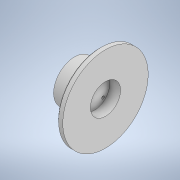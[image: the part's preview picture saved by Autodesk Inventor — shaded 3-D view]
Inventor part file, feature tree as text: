
AUTODESK INVENTOR PART (.ipt)
format: ipt  version: 2021 (Build 250183000, 183)  size: 325,120 bytes
history: native  units: mm
features: sketch x3, extrude x2, revolve x1, plane x1, pattern_circular x1
ambient origin geometry x8: Origin, YZ Plane, XZ Plane, XY Plane, X Axis, Y Axis, Z Axis, Center Point
bodies: Solid1 (feature_tree)
feature tree (8):
  revolve  "Revolution1"  [1 undecoded]
  plane  "Work Plane1"
  extrude  "Extrusion1"  Depth=2.0mm
  pattern_circular  "Circular Pattern1"  [2 undecoded]
  extrude  "Extrusion2"  Depth=10.0mm
  sketch  "Sketch1"  dims[d0=25.0mm d1=30.0mm]
  sketch  "Sketch2"  dims[d2=2.0mm d3=2.0mm]
  sketch  "Sketch3"  dims[d4=2.0mm d5=4.0mm d6=5.0mm d7=45.0mm d8=18.0mm d9=24.0mm d10=90.0deg d11=30.0mm d12=3.0mm d13=1.0mm d14=1.0mm d15=1.0mm d16=0.0mm d17=0.0mm d18=360.0mm d19=360.0deg d21=20.0mm d22=20.0mm d23=10.0mm d24=10.0mm d25=3.2mm d27=0.0mm d28=0.0mm]
note: 3 required parameter values undecoded (feature->parameter linkage not recoverable at this tier; creation-order binding heuristic only, values carry confidence <= 0.55)